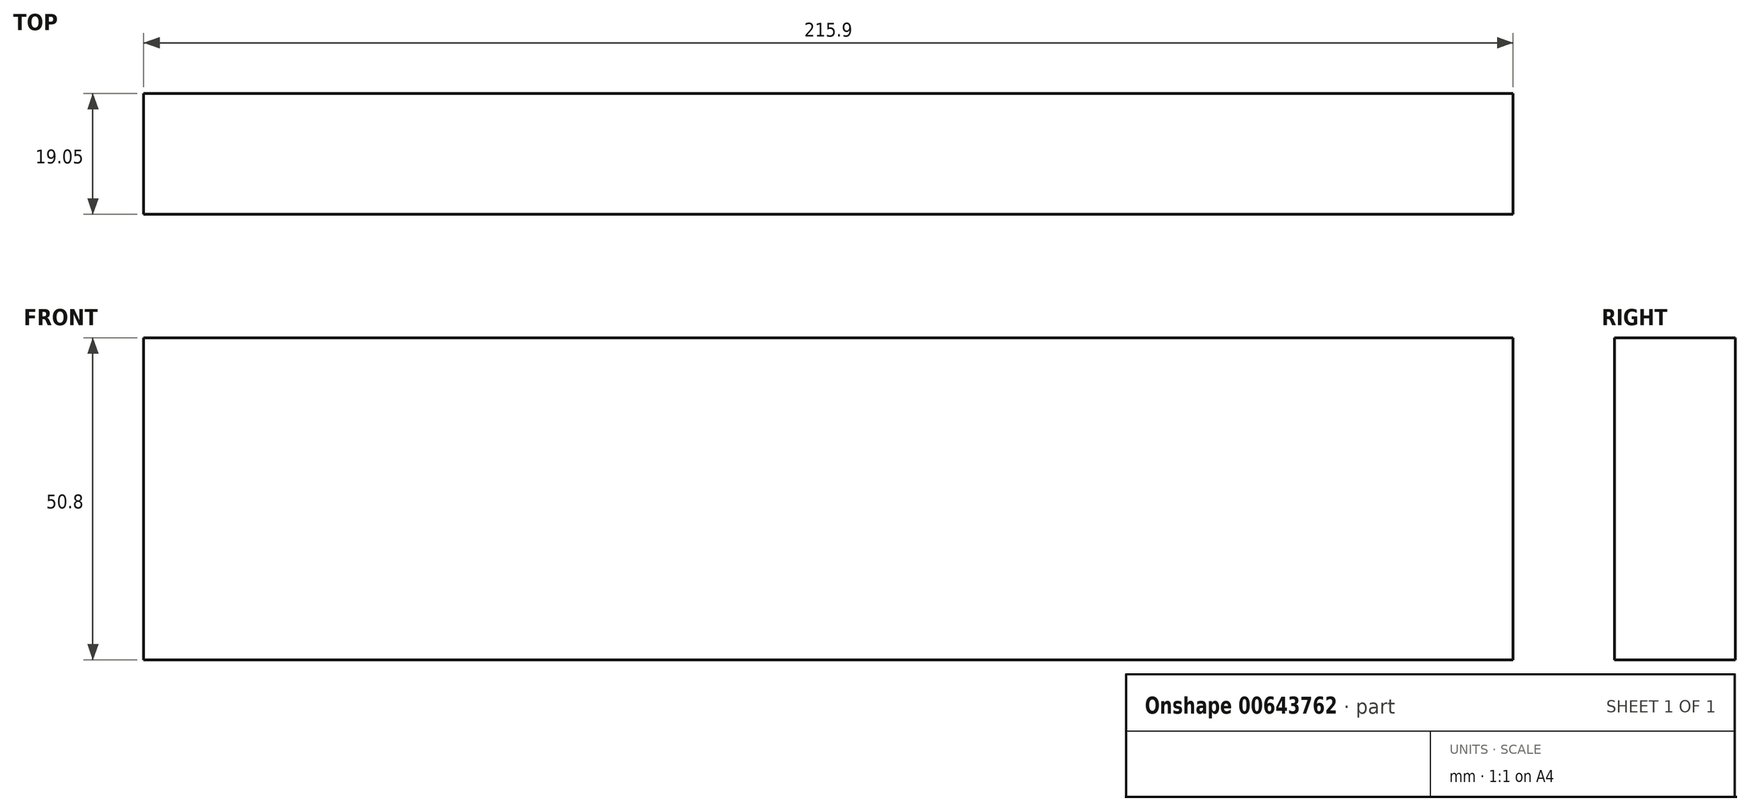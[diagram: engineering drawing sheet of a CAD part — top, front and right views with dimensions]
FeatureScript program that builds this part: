
annotation { "Feature Type Name" : "Feature", "Feature Type Description" : "" }
export const myFeature = defineFeature(function(context is Context, id is Id, definition is map)
    precondition{}
    {
        {
            var Q0;
            Q0=qCreatedBy(makeId("Front.planeOp"),FACE);
            var sketch = newSketch(context, id + "F0", { "sketchPlane" : qUnion([Q0])});
            skLineSegment(sketch, "E0.bottom", {"start": v(0, 0) * mm, "end": v(215.9, 0) * mm});
            skLineSegment(sketch, "E0.top", {"start": v(0, -50.8) * mm, "end": v(215.9, -50.8) * mm});
            skLineSegment(sketch, "E0.left", {"start": v(0, 0) * mm, "end": v(0, -50.8) * mm});
            skLineSegment(sketch, "E0.right", {"start": v(215.9, 0) * mm, "end": v(215.9, -50.8) * mm});
            skSolve(sketch);
        }
        {
            var Q0;
            Q0=makeQuery(id+"F0.imprint","IMPRINT",FACE,{"disambiguationData":[TD([[makeQuery(id+"F0.imprint","IMPRINT",EDGE,{"derivedFrom":sQuery(id+"F0.wireOp",EDGE,"E0.bottom")}),-1.0]])]});
            extrude(context, id + "F1", {"entities" : qUnion([Q0]), "depth" : 19.05 * mm, "offsetDistance" : 25.4 * mm});
        }
    });
